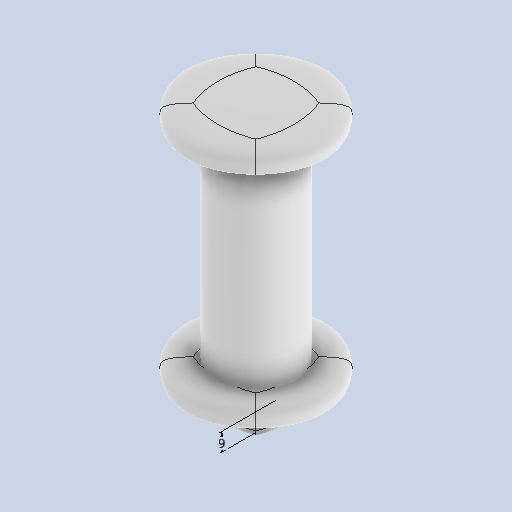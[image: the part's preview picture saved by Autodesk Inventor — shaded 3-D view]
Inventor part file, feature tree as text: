
AUTODESK INVENTOR PART (.ipt)
format: ipt  version: 2025 (Build 290162010, 162A)  size: 541,696 bytes
history: native  units: mm
features: sketch x5, extrude x4, other x2, hole x2, fillet x1, chamfer x1
ambient origin geometry x8: Origin, YZ Plane, XZ Plane, XY Plane, X Axis, Y Axis, Z Axis, Center Point
bodies: Volumenkörper5 (feature_tree), Volumenkörper6 (feature_tree), Volumenkörper8 (feature_tree)
feature tree (15):
  extrude  "Extrusion4"  Depth=100.0mm TaperAngle=0.0deg
  other  "Form5"
  other  "Form7"
  extrude  "Extrusion5"  Depth=20.0mm
  extrude  "Extrusion7"  Depth=204.0mm TaperAngle=0.0deg
  extrude  "Extrusion6"  Depth=4.0mm
  fillet  "Rundung2"  Radius=9.0mm
  sketch  "Skizze10"  dims[d50=2.459mm d51=6.0mm d52=6.3mm d53=2.0mm d54=90.0deg d55=5.0mm d56=20.594885mm d57=3.2mm d58=9.0mm d59=6.3mm d60=2.0mm d61=90.0deg d62=8.0mm d63=20.594885mm d64=2.0mm d65=2.0mm d66=45.0deg]
  hole  "Bohrung3"  [1 undecoded]
  hole  "Bohrung4"  [1 undecoded]
  chamfer  "Fasen2"  [1 undecoded]
  sketch  "Skizze6"  dims[d35=40.0mm d36=100.0mm d37=0.0mm]
  sketch  "Skizze7"  dims[d38=5.0mm d39=105.0mm d40=0.0mm d41=0.0mm d42=20.0mm]
  sketch  "Skizze8"  dims[d43=20.0mm d44=204.0mm d45=0.0mm]
  sketch  "Skizze9"  dims[d46=18.0mm d47=0.0mm d48=4.0mm d49=9.0mm]
note: 3 required parameter values undecoded (feature->parameter linkage not recoverable at this tier; creation-order binding heuristic only, values carry confidence <= 0.55)
